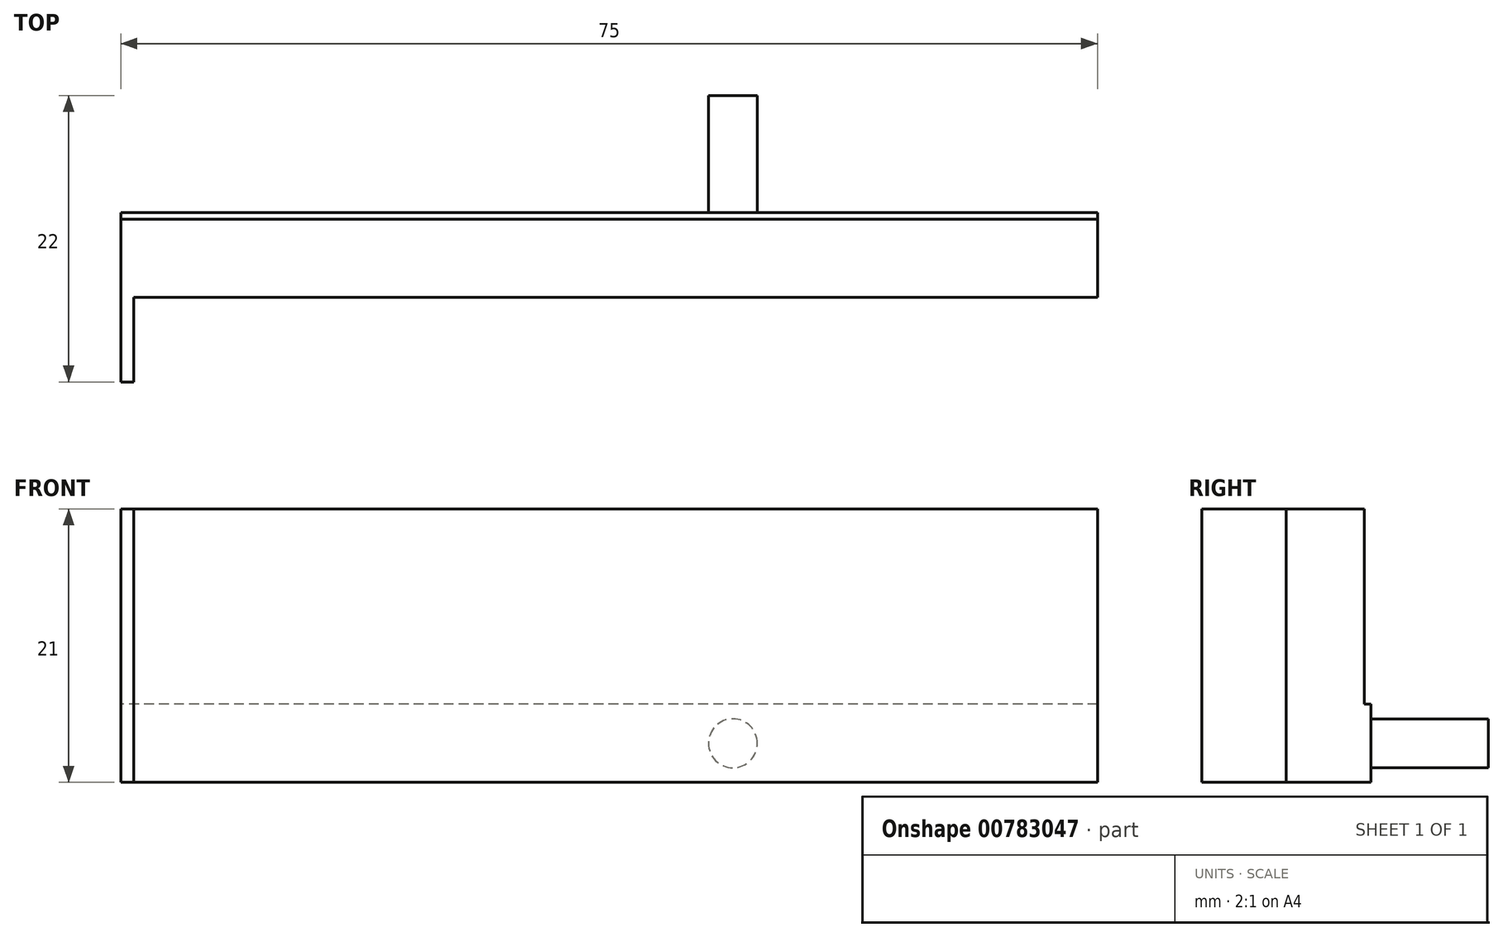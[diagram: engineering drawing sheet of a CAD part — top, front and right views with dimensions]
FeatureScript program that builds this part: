
annotation { "Feature Type Name" : "Feature", "Feature Type Description" : "" }
export const myFeature = defineFeature(function(context is Context, id is Id, definition is map)
    precondition{}
    {
        {
            var Q0;
            Q0=qCreatedBy(makeId("Right.planeOp"),FACE);
            var sketch = newSketch(context, id + "F0", { "sketchPlane" : qUnion([Q0])});
            skLineSegment(sketch, "E0", {"start": v(14.98, 53.88) * mm, "end": v(14.98, -37.12) * mm});
            skLineSegment(sketch, "E1", {"start": v(-0.52, -37.12) * mm, "end": v(14.98, -37.12) * mm});
            skLineSegment(sketch, "E2", {"start": v(-0.52, -37.12) * mm, "end": v(-0.52, -16.12) * mm});
            skLineSegment(sketch, "E3", {"start": v(5.48, -16.12) * mm, "end": v(5.48, -31.12) * mm});
            skLineSegment(sketch, "E4", {"start": v(5.48, -31.12) * mm, "end": v(8.98, -31.12) * mm});
            skLineSegment(sketch, "E5", {"start": v(8.98, -31.12) * mm, "end": v(8.98, 53.88) * mm});
            skLineSegment(sketch, "E6", {"start": v(8.98, 53.88) * mm, "end": v(14.98, 53.88) * mm});
            skLineSegment(sketch, "E7", {"start": v(-0.52, -16.12) * mm, "end": v(5.48, -16.12) * mm});
            skSolve(sketch);
        }
        {
            var Q0;
            Q0=makeQuery(id+"F0.imprint","IMPRINT",FACE,{"disambiguationData":[TD([[makeQuery(id+"F0.imprint","IMPRINT",EDGE,{"derivedFrom":sQuery(id+"F0.wireOp",EDGE,"E0")}),-1.0]])]});
            extrude(context, id + "F1", {"entities" : qUnion([Q0]), "depth" : 67 * mm, "offsetDistance" : 25 * mm});
        }
        {
            var Q0;
            Q0=makeQuery(id+"F1.opExtrude","CAP_FACE",FACE,{"disambiguationData":[OSD([sQuery(id+"F0.wireOp",EDGE,"E0"),sQuery(id+"F0.wireOp",EDGE,"E1"),sQuery(id+"F0.wireOp",EDGE,"E2"),sQuery(id+"F0.wireOp",EDGE,"E3"),sQuery(id+"F0.wireOp",EDGE,"E4"),sQuery(id+"F0.wireOp",EDGE,"E5"),sQuery(id+"F0.wireOp",EDGE,"E6"),sQuery(id+"F0.wireOp",EDGE,"E7")])],"isStart":false});
            var sketch = newSketch(context, id + "F2", { "sketchPlane" : qUnion([Q0])});
            skCircle(sketch, "E8", {"center": v(11.98, 43.88) * mm, "radius": 1.5 * mm});
            skCircle(sketch, "E9", {"center": v(11.98, 23.88) * mm, "radius": 1.5 * mm});
            skCircle(sketch, "E10.MirrorC", {"center": v(11.98, -27.12) * mm, "radius": 1.5 * mm});
            skCircle(sketch, "E11.MirrorC", {"center": v(11.98, -7.12) * mm, "radius": 1.5 * mm});
            skLineSegment(sketch, "E12", {"start": v(11.98, 43.88) * mm, "end": v(11.98, 53.88) * mm});
            skLineSegment(sketch, "E13", {"start": v(11.98, 43.88) * mm, "end": v(11.98, 23.88) * mm});
            skSolve(sketch);
        }
        {
            var Q0;
            Q0=makeQuery(id+"F2.imprint","IMPRINT",FACE,{"disambiguationData":[TD([[makeQuery(id+"F2.imprint","IMPRINT",EDGE,{"derivedFrom":sQuery(id+"F2.wireOp",EDGE,"E8")}),1.0]])]});
            var Q1;
            Q1=makeQuery(id+"F2.imprint","IMPRINT",FACE,{"disambiguationData":[TD([[makeQuery(id+"F2.imprint","IMPRINT",EDGE,{"derivedFrom":sQuery(id+"F2.wireOp",EDGE,"E9")}),1.0]])]});
            var Q2;
            Q2=makeQuery(id+"F2.imprint","IMPRINT",FACE,{"disambiguationData":[TD([[makeQuery(id+"F2.imprint","IMPRINT",EDGE,{"derivedFrom":sQuery(id+"F2.wireOp",EDGE,"E11.MirrorC")}),-1.0]])]});
            var Q3;
            Q3=makeQuery(id+"F2.imprint","IMPRINT",FACE,{"disambiguationData":[TD([[makeQuery(id+"F2.imprint","IMPRINT",EDGE,{"derivedFrom":sQuery(id+"F2.wireOp",EDGE,"E10.MirrorC")}),-1.0]])]});
            extrude(context, id + "F3", {"entities" : qUnion([Q0, Q1, Q2, Q3]), "operationType" : NewBodyOperationType.ADD, "depth" : 8 * mm, "offsetDistance" : 25 * mm});
        }
        {
            var Q0;
            Q0=makeQuery(id+"F1.opExtrude","CAP_FACE",FACE,{"disambiguationData":[OSD([sQuery(id+"F0.wireOp",EDGE,"E0"),sQuery(id+"F0.wireOp",EDGE,"E1"),sQuery(id+"F0.wireOp",EDGE,"E2"),sQuery(id+"F0.wireOp",EDGE,"E3"),sQuery(id+"F0.wireOp",EDGE,"E4"),sQuery(id+"F0.wireOp",EDGE,"E5"),sQuery(id+"F0.wireOp",EDGE,"E6"),sQuery(id+"F0.wireOp",EDGE,"E7")])],"isStart":true});
            var sketch = newSketch(context, id + "F4", { "sketchPlane" : qUnion([Q0])});
            skCircle(sketch, "E14", {"center": v(-18.48, 43.88) * mm, "radius": 1.88 * mm});
            skCircle(sketch, "E15", {"center": v(-18.48, 23.88) * mm, "radius": 1.88 * mm});
            skCircle(sketch, "E16.MirrorC", {"center": v(-18.48, -27.12) * mm, "radius": 1.88 * mm});
            skCircle(sketch, "E17.MirrorC", {"center": v(-18.48, -7.12) * mm, "radius": 1.88 * mm});
            skSolve(sketch);
        }
        {
            var Q0;
            Q0=makeQuery(id+"F4.imprint","IMPRINT",FACE,{"disambiguationData":[TD([[makeQuery(id+"F4.imprint","IMPRINT",EDGE,{"derivedFrom":sQuery(id+"F4.wireOp",EDGE,"E15")}),1.0]])]});
            var Q1;
            Q1=makeQuery(id+"F4.imprint","IMPRINT",FACE,{"disambiguationData":[TD([[makeQuery(id+"F4.imprint","IMPRINT",EDGE,{"derivedFrom":sQuery(id+"F4.wireOp",EDGE,"E14")}),1.0]])]});
            var Q2;
            Q2=makeQuery(id+"F4.imprint","IMPRINT",FACE,{"disambiguationData":[TD([[makeQuery(id+"F4.imprint","IMPRINT",EDGE,{"derivedFrom":sQuery(id+"F4.wireOp",EDGE,"E17.MirrorC")}),-1.0]])]});
            var Q3;
            Q3=makeQuery(id+"F4.imprint","IMPRINT",FACE,{"disambiguationData":[TD([[makeQuery(id+"F4.imprint","IMPRINT",EDGE,{"derivedFrom":sQuery(id+"F4.wireOp",EDGE,"E16.MirrorC")}),-1.0]])]});
            extrude(context, id + "F5", {"entities" : qUnion([Q0, Q1, Q2, Q3]), "operationType" : NewBodyOperationType.REMOVE, "oppositeDirection" : true, "depth" : 9 * mm, "offsetDistance" : 25 * mm});
        }
        {
            var Q0;
            Q0=makeQuery(id+"F1.opExtrude","SWEPT_FACE",FACE,{"disambiguationData":[OSD([sQuery(id+"F0.wireOp",EDGE,"E0")])]});
            var sketch = newSketch(context, id + "F6", { "sketchPlane" : qUnion([Q0])});
            skLineSegment(sketch, "E18", {"start": v(0, -37.12) * mm, "end": v(0, -34.12) * mm});
            skCircle(sketch, "E19", {"center": v(-20, -34.12) * mm, "radius": 1.88 * mm});
            skCircle(sketch, "E20.MirrorC", {"center": v(-47, -34.12) * mm, "radius": 1.88 * mm});
            skSolve(sketch);
        }
        {
            var Q0;
            Q0=makeQuery(id+"F6.imprint","IMPRINT",FACE,{"disambiguationData":[TD([[makeQuery(id+"F6.imprint","IMPRINT",EDGE,{"derivedFrom":sQuery(id+"F6.wireOp",EDGE,"E20.MirrorC")}),-1.0]])]});
            var Q1;
            Q1=makeQuery(id+"F6.imprint","IMPRINT",FACE,{"disambiguationData":[TD([[makeQuery(id+"F6.imprint","IMPRINT",EDGE,{"derivedFrom":sQuery(id+"F6.wireOp",EDGE,"064d96a8-f5e3-4a6a-84b9-f8e9dd95ac0b0.MirrorC")}),-1.0]])]});
            var Q2;
            Q2=makeQuery(id+"F6.imprint","IMPRINT",FACE,{"disambiguationData":[TD([[makeQuery(id+"F6.imprint","IMPRINT",EDGE,{"derivedFrom":sQuery(id+"F6.wireOp",EDGE,"sfNKTgSD-Wn5j-8V8k-rCBi-PUns8C3nGana")}),1.0]])]});
            var Q3;
            Q3=makeQuery(id+"F6.imprint","IMPRINT",FACE,{"disambiguationData":[TD([[makeQuery(id+"F6.imprint","IMPRINT",EDGE,{"derivedFrom":sQuery(id+"F6.wireOp",EDGE,"E19")}),1.0]])]});
            extrude(context, id + "F7", {"entities" : qUnion([Q0, Q1, Q2, Q3]), "operationType" : NewBodyOperationType.REMOVE, "oppositeDirection" : true, "depth" : 9 * mm, "offsetDistance" : 25 * mm});
        }
        {
            var Q0;
            Q0=makeQuery(id+"F1.opExtrude","SWEPT_FACE",FACE,{"disambiguationData":[OSD([sQuery(id+"F0.wireOp",EDGE,"E2")])]});
            var sketch = newSketch(context, id + "F8", { "sketchPlane" : qUnion([Q0])});
            skLineSegment(sketch, "E21.bottom", {"start": v(0, -16.12) * mm, "end": v(1, -16.12) * mm});
            skLineSegment(sketch, "E21.top", {"start": v(0, -37.12) * mm, "end": v(1, -37.12) * mm});
            skLineSegment(sketch, "E21.left", {"start": v(0, -16.12) * mm, "end": v(0, -37.12) * mm});
            skLineSegment(sketch, "E21.right", {"start": v(1, -16.12) * mm, "end": v(1, -37.12) * mm});
            skSolve(sketch);
        }
        {
            var Q0;
            Q0=makeQuery(id+"F8.imprint","IMPRINT",FACE,{"disambiguationData":[TD([[makeQuery(id+"F8.imprint","IMPRINT",EDGE,{"derivedFrom":sQuery(id+"F8.wireOp",EDGE,"E21.bottom")}),1.0]])]});
            extrude(context, id + "F9", {"entities" : qUnion([Q0]), "operationType" : NewBodyOperationType.ADD, "depth" : 6.5 * mm, "offsetDistance" : 25 * mm});
        }
        {
            var Q0;
            Q0=makeQuery(id+"F9.boolean.opBoolean","MERGE",FACE,{"derivedFrom":[makeQuery(id+"F1.opExtrude","CAP_FACE",FACE,{"disambiguationData":[OSD([sQuery(id+"F0.wireOp",EDGE,"E0"),sQuery(id+"F0.wireOp",EDGE,"E1"),sQuery(id+"F0.wireOp",EDGE,"E2"),sQuery(id+"F0.wireOp",EDGE,"E3"),sQuery(id+"F0.wireOp",EDGE,"E4"),sQuery(id+"F0.wireOp",EDGE,"E5"),sQuery(id+"F0.wireOp",EDGE,"E6"),sQuery(id+"F0.wireOp",EDGE,"E7")])],"isStart":true}),makeQuery(id+"F9.opExtrude","SWEPT_FACE",FACE,{"disambiguationData":[OSD([sQuery(id+"F8.wireOp",EDGE,"E21.left")])]})]});
            var sketch = newSketch(context, id + "F10", { "sketchPlane" : qUnion([Q0])});
            skLineSegment(sketch, "E22", {"start": v(-11.98, 53.88) * mm, "end": v(-11.98, 43.88) * mm});
            skLineSegment(sketch, "E23", {"start": v(-11.98, 43.88) * mm, "end": v(-11.98, 23.88) * mm});
            skCircle(sketch, "E24", {"center": v(-11.98, 43.88) * mm, "radius": 1.88 * mm});
            skCircle(sketch, "E25", {"center": v(-11.98, 23.88) * mm, "radius": 1.88 * mm});
            skCircle(sketch, "E26.MirrorC", {"center": v(-11.98, -27.12) * mm, "radius": 1.88 * mm});
            skCircle(sketch, "E27.MirrorC", {"center": v(-11.98, -7.12) * mm, "radius": 1.88 * mm});
            skSolve(sketch);
        }
        {
            var Q0;
            Q0 = qSketchRegion(id + "F10", true);
            extrude(context, id + "F11", {"entities" : qUnion([Q0]), "operationType" : NewBodyOperationType.REMOVE, "oppositeDirection" : true, "depth" : 9 * mm, "offsetDistance" : 25 * mm});
        }
    });
